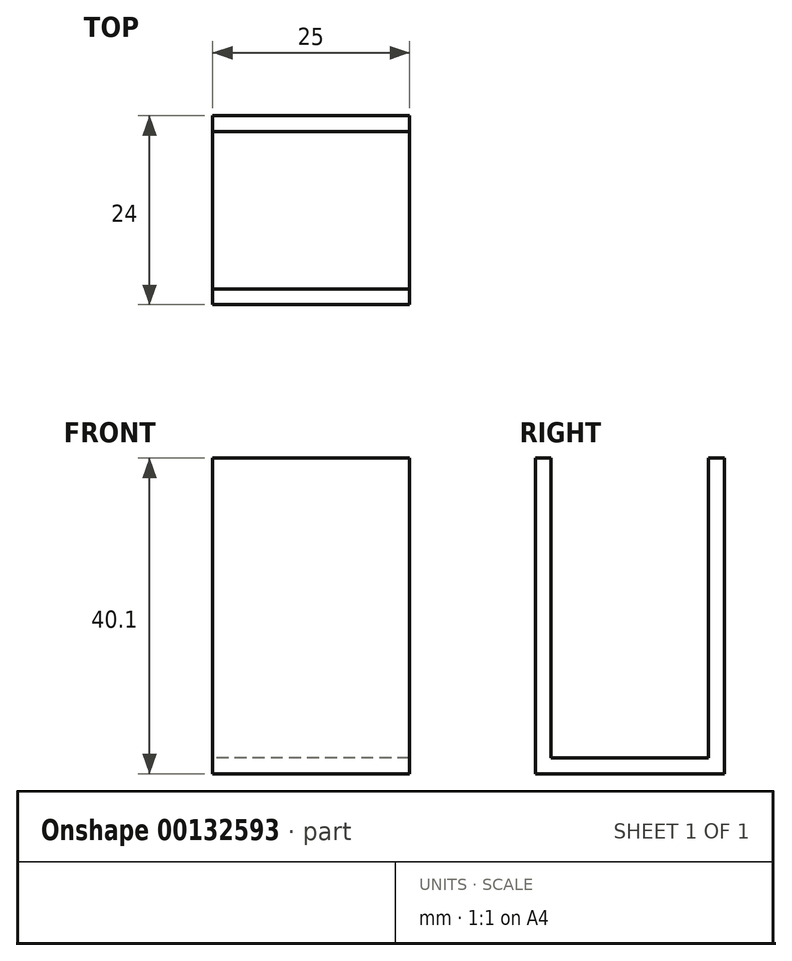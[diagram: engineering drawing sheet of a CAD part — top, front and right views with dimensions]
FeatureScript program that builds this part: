
annotation { "Feature Type Name" : "Feature", "Feature Type Description" : "" }
export const myFeature = defineFeature(function(context is Context, id is Id, definition is map)
    precondition{}
    {
        {
            var Q0;
            Q0=qCreatedBy(makeId("Top.planeOp"),FACE);
            var sketch = newSketch(context, id + "F0", { "sketchPlane" : qUnion([Q0])});
            skLineSegment(sketch, "E0.bottom", {"start": v(14.5, 12) * mm, "end": v(-14.5, 12) * mm});
            skLineSegment(sketch, "E0.top", {"start": v(14.5, -12) * mm, "end": v(-14.5, -12) * mm});
            skLineSegment(sketch, "E0.left", {"start": v(14.5, 12) * mm, "end": v(14.5, -12) * mm});
            skLineSegment(sketch, "E0.right", {"start": v(-14.5, 12) * mm, "end": v(-14.5, -12) * mm});
            skPoint(sketch, "E0.middle", {"position": v(0, 0) * mm});
            skLineSegment(sketch, "E1.bottom", {"start": v(12.5, 10) * mm, "end": v(-12.5, 10) * mm});
            skLineSegment(sketch, "E1.top", {"start": v(12.5, -10) * mm, "end": v(-12.5, -10) * mm});
            skLineSegment(sketch, "E1.left", {"start": v(12.5, 10) * mm, "end": v(12.5, -10) * mm});
            skLineSegment(sketch, "E1.right", {"start": v(-12.5, 10) * mm, "end": v(-12.5, -10) * mm});
            skSolve(sketch);
        }
        {
            var Q0;
            Q0=makeQuery(id+"F0.imprint","IMPRINT",FACE,{"disambiguationData":[TD([[makeQuery(id+"F0.imprint","IMPRINT",EDGE,{"derivedFrom":sQuery(id+"F0.wireOp",EDGE,"E0.bottom")}),1.0]])]});
            extrude(context, id + "F1", {"entities" : qUnion([Q0]), "depth" : 38.1 * mm});
        }
        {
            var Q0;
            Q0=makeQuery(id+"F0.imprint","IMPRINT",FACE,{"disambiguationData":[TD([[makeQuery(id+"F0.imprint","IMPRINT",EDGE,{"derivedFrom":sQuery(id+"F0.wireOp",EDGE,"E1.bottom")}),1.0]])]});
            var Q1;
            Q1=makeQuery(id+"F0.imprint","IMPRINT",FACE,{"disambiguationData":[TD([[makeQuery(id+"F0.imprint","IMPRINT",EDGE,{"derivedFrom":sQuery(id+"F0.wireOp",EDGE,"E0.bottom")}),1.0]])]});
            extrude(context, id + "F2", {"entities" : qUnion([Q0, Q1]), "operationType" : NewBodyOperationType.ADD, "oppositeDirection" : true, "depth" : 2 * mm});
        }
        {
            var Q0;
            {var subQ0=sQuery(id+"F0.wireOp",EDGE,"E0.right");Q0=makeQuery(id+"F2.boolean.opBoolean","MERGE",FACE,{"derivedFrom":[makeQuery(id+"F1.opExtrude","SWEPT_FACE",FACE,{"disambiguationData":[OSD([subQ0])]}),makeQuery(id+"F2.opExtrude","SWEPT_FACE",FACE,{"disambiguationData":[OSD([subQ0])]})]});}
            var sketch = newSketch(context, id + "F3", { "sketchPlane" : qUnion([Q0])});
            skLineSegment(sketch, "E2.bottom", {"start": v(-10, 38.1) * mm, "end": v(10, 38.1) * mm});
            skLineSegment(sketch, "E2.top", {"start": v(-10, 0) * mm, "end": v(10, 0) * mm});
            skLineSegment(sketch, "E2.left", {"start": v(-10, 38.1) * mm, "end": v(-10, 0) * mm});
            skLineSegment(sketch, "E2.right", {"start": v(10, 38.1) * mm, "end": v(10, 0) * mm});
            skSolve(sketch);
        }
        {
            var Q0;
            Q0=makeQuery(id+"F3.imprint","IMPRINT",FACE,{"disambiguationData":[TD([[makeQuery(id+"F3.imprint","IMPRINT",EDGE,{"derivedFrom":sQuery(id+"F3.wireOp",EDGE,"E2.bottom")}),-1.0]])]});
            extrude(context, id + "F4", {"entities" : qUnion([Q0]), "operationType" : NewBodyOperationType.REMOVE, "endBound" : BoundingType.THROUGH_ALL, "oppositeDirection" : true, "depth" : 2 * mm});
        }
        {
            var Q0;
            Q0=makeQuery(id+"F2.opExtrude","CAP_FACE",FACE,{"disambiguationData":[OSD([sQuery(id+"F0.wireOp",EDGE,"E0.bottom"),sQuery(id+"F0.wireOp",EDGE,"E0.top"),sQuery(id+"F0.wireOp",EDGE,"E0.left"),sQuery(id+"F0.wireOp",EDGE,"E0.right")])],"isStart":false});
            var sketch = newSketch(context, id + "F5", { "sketchPlane" : qUnion([Q0])});
            skLineSegment(sketch, "E3.bottom", {"start": v(14.5, 12) * mm, "end": v(-14.5, 12) * mm});
            skLineSegment(sketch, "E3.top", {"start": v(14.5, -12) * mm, "end": v(-14.5, -12) * mm});
            skLineSegment(sketch, "E3.left", {"start": v(14.5, 12) * mm, "end": v(14.5, -12) * mm});
            skLineSegment(sketch, "E3.right", {"start": v(-14.5, 12) * mm, "end": v(-14.5, -12) * mm});
            skPoint(sketch, "E3.middle", {"position": v(0, 0) * mm});
            skLineSegment(sketch, "E4.bottom", {"start": v(12.5, 10) * mm, "end": v(-12.5, 10) * mm});
            skLineSegment(sketch, "E4.top", {"start": v(12.5, -10) * mm, "end": v(-12.5, -10) * mm});
            skLineSegment(sketch, "E4.left", {"start": v(12.5, 10) * mm, "end": v(12.5, -10) * mm});
            skLineSegment(sketch, "E4.right", {"start": v(-12.5, 10) * mm, "end": v(-12.5, -10) * mm});
            skLineSegment(sketch, "E5", {"start": v(-12.5, 10) * mm, "end": v(-12.5, 12) * mm});
            skLineSegment(sketch, "E6", {"start": v(12.5, -10) * mm, "end": v(12.5, -12) * mm});
            skLineSegment(sketch, "E7", {"start": v(12.5, 10) * mm, "end": v(12.5, 12) * mm});
            skLineSegment(sketch, "E8", {"start": v(-12.5, -12) * mm, "end": v(-12.5, -10) * mm});
            skSolve(sketch);
        }
        {
            var Q0;
            {var subQ0=sQuery(id+"F5.wireOp",EDGE,"E3.right");Q0=makeQuery(id+"F5.imprint","IMPRINT",FACE,{"disambiguationData":[TD([[makeQuery(id+"F5.imprint","IMPRINT",EDGE,{"derivedFrom":subQ0}),-1.0]])]});}
            var Q1;
            {var subQ0=sQuery(id+"F5.wireOp",EDGE,"E3.left");Q1=makeQuery(id+"F5.imprint","IMPRINT",FACE,{"disambiguationData":[TD([[makeQuery(id+"F5.imprint","IMPRINT",EDGE,{"derivedFrom":subQ0}),1.0]])]});}
            extrude(context, id + "F6", {"entities" : qUnion([Q0, Q1]), "operationType" : NewBodyOperationType.REMOVE, "endBound" : BoundingType.THROUGH_ALL, "oppositeDirection" : true, "depth" : 25.4 * mm});
        }
    });
